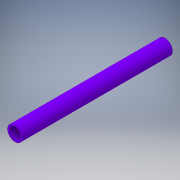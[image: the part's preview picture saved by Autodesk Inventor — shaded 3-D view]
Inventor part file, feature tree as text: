
AUTODESK INVENTOR PART (.ipt)
format: ipt  version: 2018 (Build 220112000, 112)  size: 105,984 bytes
history: native  units: in
note: dims shown in document units (in); Inventor stores cm internally (conversion verified against a paired STEP export)
features: extrude x1, sketch x1
ambient origin geometry x8: Origin, YZ Plane, XZ Plane, XY Plane, X Axis, Y Axis, Z Axis, Center Point
bodies: Solid1 (feature_tree)
feature tree (2):
  extrude  "Extrusion1"  Depth=13.1875in
  sketch  "Sketch1"  dims[d0=1.315in d1=1.0in d2=13.1875in d3=0.0in]
